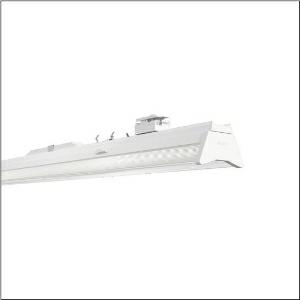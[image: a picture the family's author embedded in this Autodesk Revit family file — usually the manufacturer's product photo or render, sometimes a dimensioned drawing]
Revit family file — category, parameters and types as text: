
# Revit family: licross_11_performance_mo_51td16dn4axg
name_source: partatom
category: Lighting Fixtures
units: mm (PartAtom-declared; Revit-internal decimal feet)

## family parameters
Cut with Voids When Loaded = No
Host = Face
Light Source = No
Part Type = Normal
Room Calculation Point = No
Round Connector Dimension = Use Diameter
Shared = No

## types (1)
- --- (1 x LED, 10110 lm, 57.1 W, 4000K)
    Apparent Load = 57 VA
    CIE Flux Codes = 66 88 96 79 100
    Color Rendering = 80
    Color Temperature = 4000K
    Default Elevation = 1800 mm
    Description = Licross 11 Performance MO, luminaire insert, of sheet steel, galvanised, coil coated, white, length: 1.500mm, width: 120mm, height: 123mm, LED rated luminous flux: 10.110lm, light colour: 840, SDCM (Standard Deviation of Colour Matching)MacAdam ≤ 2 SDCM (initial), control gear: DALI 2, with plug, 5-pole, with phase selection, mains connection: 220..240V, AC, 50/60Hz, rated input power: 57W, internal wiring halogen-free, primary light control with lens, of plastic, primary optical cover: cover, of PMMA, light emission: direct/indirect distribution, primary light characteristic: symmetric, protection rating (complete): IP54, insulation class (complete): insulation class I (protective earthing), certification: CE, ENEC, VDE, UKCA, protection symbol: D if used in an environment with non-conductive dust loads with corresponding accessories, impact resistance: IK06, permissible ambient temperature for indoor applications: -25..+35°C, corresponds to IFS (International Featured Standards) requirements for safety and quality in the food industry, reducing of maximum allowable ambient temperature of 5°C with ceiling mounting, LABS conformity tested according to VDMA 24364:2018-05, The light source and the operating device comply with the requirements of the Ecodesign Regulation (EU) 2019/2020 and are replaceable in accordance with this regulation, packaging unit: 1 piece
    Height = 114 mm
    Lamp = 1 x LED
    Lamp Light Flux = 10110 lm
    Lamp Power = 57.1 W
    Lamp count = 1
    Length = 1500 mm
    Luminous efficacy = 177 lm/W
    Manufacturer = Siteco
    ModVariant = No
    Model = 51TD16DN4AXG
    Mounting Place = Ceiling
    Mounting Type = Pendant
    Number of Poles = 1
    OnlyDefault = Yes
    Power Factor = 1
    Product Name = Licross 11 Performance MO
    Product group = luminaire insert | ceiling pendant
    ProductGroupID = 901
    Protection Class = Protection class I
    Protection Degree = IP 54
    RLX_Detail_Level = 1
    RLX_Emergency_Light_Flux = 0 lm
    RLX_Emergency_Type = 0
    RLX_Emergency_Type_DB = No
    RlxData = <blob elided: 34361 chars, md5=1c035fe9>
    Socket = socket
    Standby Power = 0 W
    System Light Flux = 10110 lm
    System Power = 57 W
    Type Comments = factory setting: luminous flux: 100 % | dim-lin: 254 | 378 mA
    Type Image = l_1256138.jpg
    URL = http://relux.com
    VarID = @adj_102851
    Voltage = 0 V
    Weight = 0.00 kg
    Width = 120 mm

## geometry (parser evidence)
native form markers: Blend x4, Sweep x12
no freeform markers — native parametric forms only
